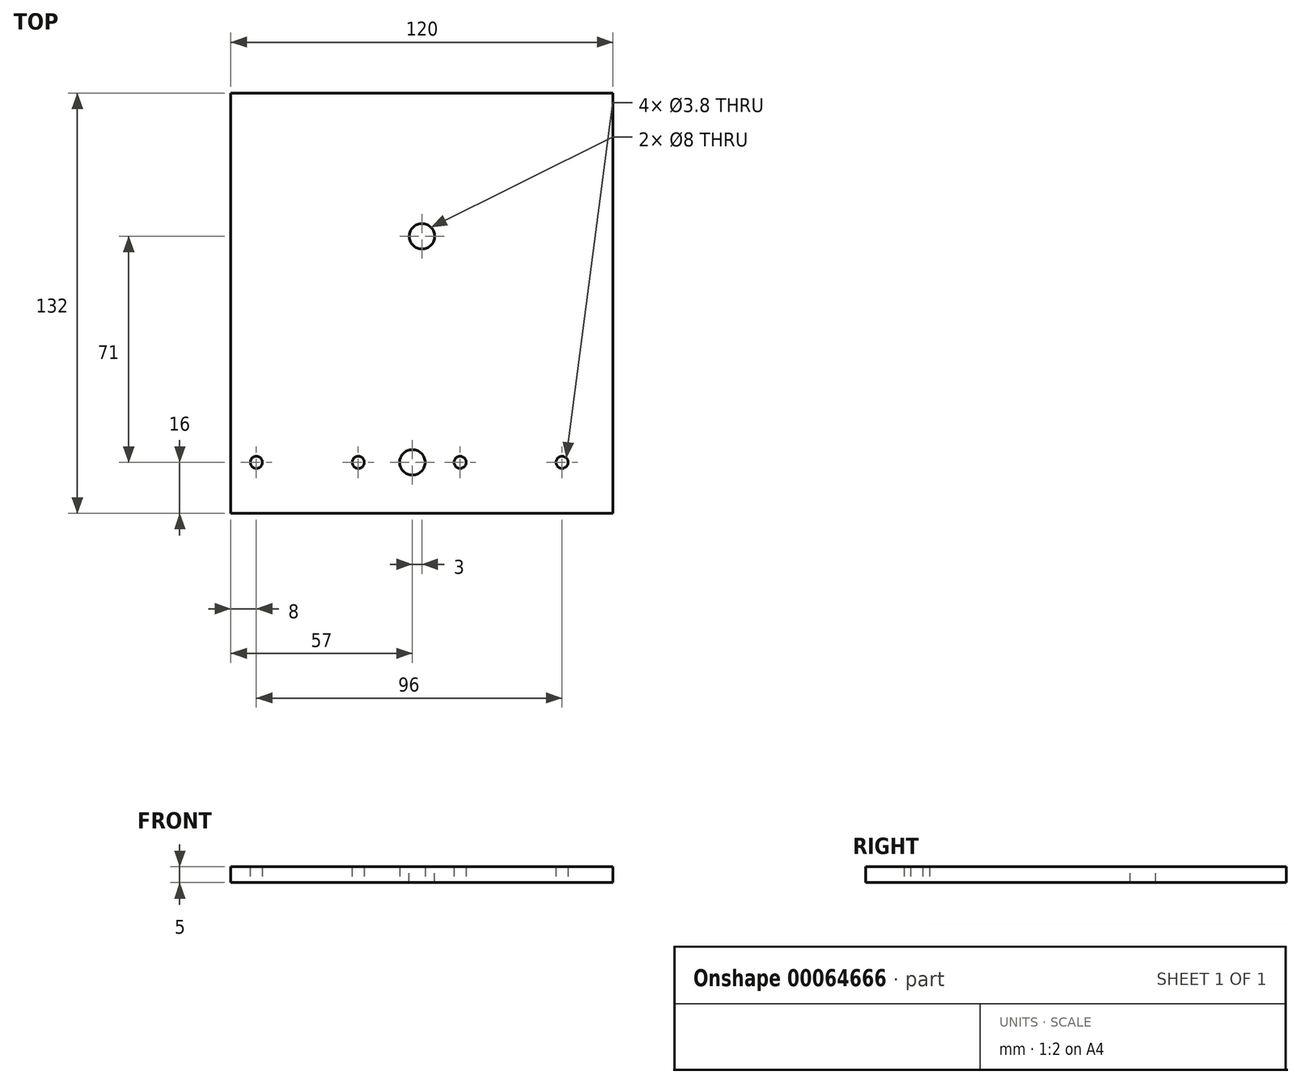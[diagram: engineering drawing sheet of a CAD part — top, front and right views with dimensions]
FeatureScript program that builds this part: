
annotation { "Feature Type Name" : "Feature", "Feature Type Description" : "" }
export const myFeature = defineFeature(function(context is Context, id is Id, definition is map)
    precondition{}
    {
        {
            var Q0;
            Q0=qCreatedBy(makeId("Top.planeOp"),FACE);
            var sketch = newSketch(context, id + "F0", { "sketchPlane" : qUnion([Q0])});
            skLineSegment(sketch, "E0.rect.bottom", {"start": v(-60, -66) * mm, "end": v(60, -66) * mm});
            skLineSegment(sketch, "E0.rect.top", {"start": v(-60, 66) * mm, "end": v(60, 66) * mm});
            skLineSegment(sketch, "E0.rect.left", {"start": v(-60, -66) * mm, "end": v(-60, 66) * mm});
            skLineSegment(sketch, "E0.rect.right", {"start": v(60, -66) * mm, "end": v(60, 66) * mm});
            skPoint(sketch, "E0.rect.middle", {"position": v(0, 0) * mm});
            skLineSegment(sketch, "E1", {"start": v(44, -66) * mm, "end": v(44, -50) * mm, "construction": true});
            skLineSegment(sketch, "E2", {"start": v(60, -66) * mm, "end": v(44, -66) * mm, "construction": true});
            skLineSegment(sketch, "E3", {"start": v(44, -50) * mm, "end": v(60, -50) * mm, "construction": true});
            skCircle(sketch, "E4", {"center": v(44, -50) * mm, "radius": 1.9 * mm});
            skCircle(sketch, "E5.1.0.0", {"center": v(12, -50) * mm, "radius": 1.9 * mm});
            skCircle(sketch, "E5.2.0.0", {"center": v(-20, -50) * mm, "radius": 1.9 * mm});
            skCircle(sketch, "E5.3.0.0", {"center": v(-52, -50) * mm, "radius": 1.9 * mm});
            skLineSegment(sketch, "E5.direction1", {"start": v(44, -50) * mm, "end": v(12, -50) * mm, "construction": true});
            skLineSegment(sketch, "E6", {"start": v(12, -50) * mm, "end": v(-3, -50) * mm, "construction": true});
            skCircle(sketch, "E7", {"center": v(-3, -50) * mm, "radius": 4 * mm});
            skSolve(sketch);
        }
        {
            var Q0;
            Q0=makeQuery(id+"F0.imprint","IMPRINT",FACE,{"disambiguationData":[TD([[makeQuery(id+"F0.imprint","IMPRINT",EDGE,{"derivedFrom":sQuery(id+"F0.wireOp",EDGE,"E0.rect.bottom")}),1.0]])]});
            var Q1;
            Q1=makeQuery(id+"F0.imprint","IMPRINT",FACE,{"disambiguationData":[TD([[makeQuery(id+"F0.imprint","IMPRINT",EDGE,{"derivedFrom":sQuery(id+"F0.wireOp",EDGE,"E0.rect.top")}),1.0]])]});
            extrude(context, id + "F1", {"entities" : qUnion([Q0, Q1]), "depth" : 5 * mm});
        }
        {
            var Q0;
            Q0=makeQuery(id+"F1.opExtrude","CAP_FACE",FACE,{"disambiguationData":[OSD([sQuery(id+"F0.wireOp",EDGE,"E0.rect.bottom"),sQuery(id+"F0.wireOp",EDGE,"E0.rect.top"),sQuery(id+"F0.wireOp",EDGE,"E0.rect.left"),sQuery(id+"F0.wireOp",EDGE,"E0.rect.right")])],"isStart":false});
            var sketch = newSketch(context, id + "F2", { "sketchPlane" : qUnion([Q0])});
            skLineSegment(sketch, "E8", {"start": v(0, 66) * mm, "end": v(0, 21) * mm, "construction": true});
            skPoint(sketch, "E8.endSnap0", {"position": v(0, 66) * mm});
            skCircle(sketch, "E9", {"center": v(0, 21) * mm, "radius": 4 * mm});
            skSolve(sketch);
        }
        {
            var Q0;
            Q0=makeQuery(id+"F2.imprint","IMPRINT",FACE,{"disambiguationData":[TD([[makeQuery(id+"F2.imprint","IMPRINT",EDGE,{"derivedFrom":sQuery(id+"F2.wireOp",EDGE,"E9")}),1.0]])]});
            var Q1;
            Q1=makeQuery(id+"F2.imprint","IMPRINT",FACE,{"disambiguationData":[TD([[makeQuery(id+"F2.imprint","IMPRINT",EDGE,{"derivedFrom":sQuery(id+"F2.wireOp",EDGE,"1bce6a2f-d512-4ec6-a197-546a77cf71d6")}),1.0]])]});
            extrude(context, id + "F3", {"entities" : qUnion([Q0, Q1]), "operationType" : NewBodyOperationType.REMOVE, "oppositeDirection" : true, "depth" : 25 * mm});
        }
    });
